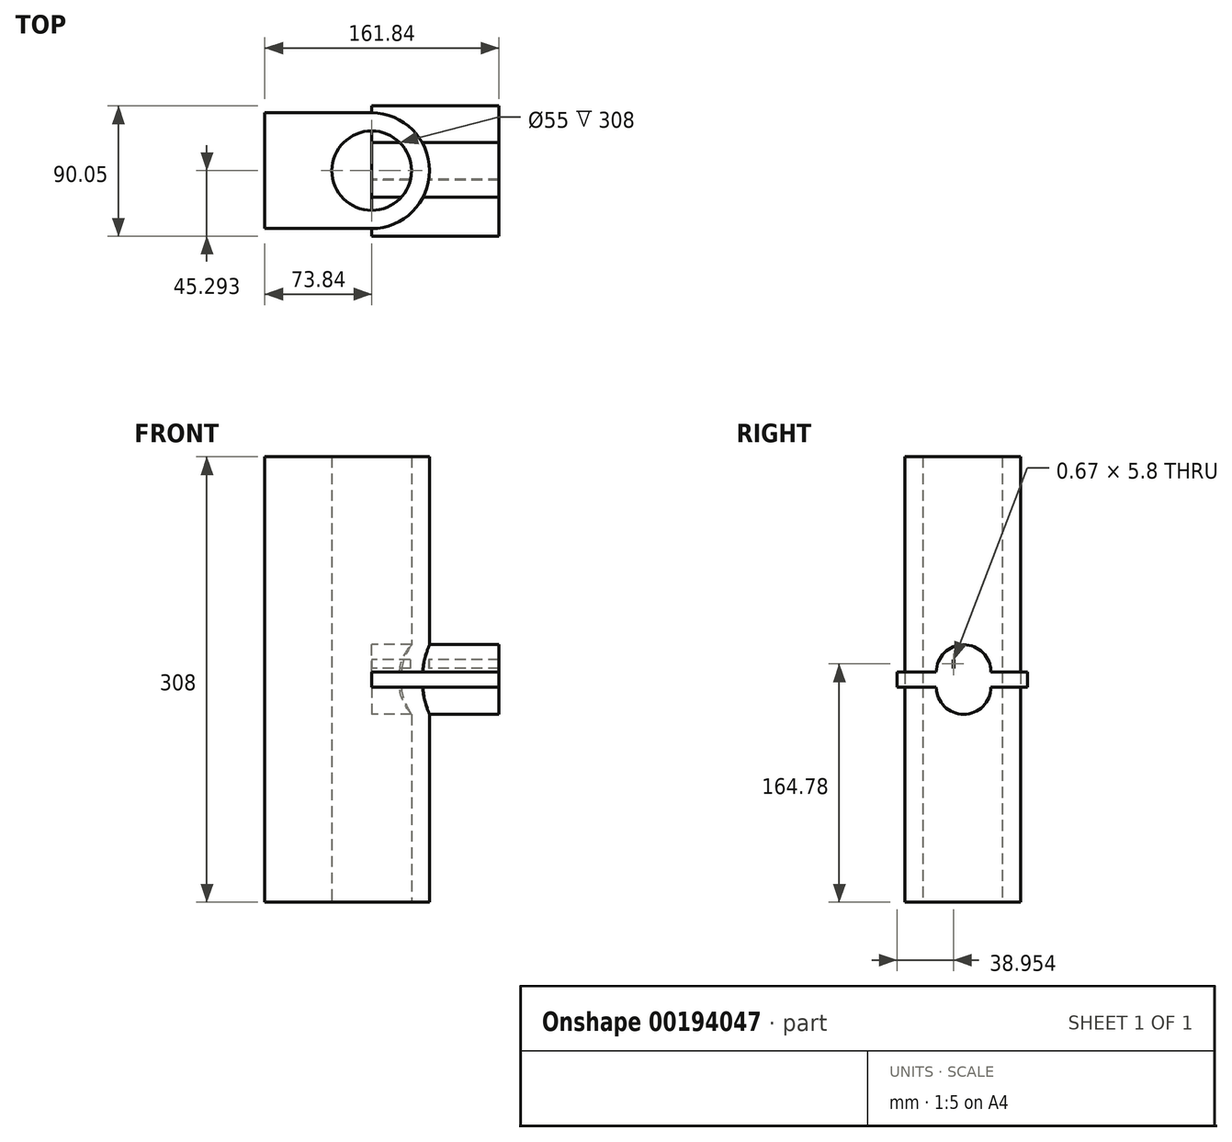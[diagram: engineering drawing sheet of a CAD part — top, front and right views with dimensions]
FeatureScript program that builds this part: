
annotation { "Feature Type Name" : "Feature", "Feature Type Description" : "" }
export const myFeature = defineFeature(function(context is Context, id is Id, definition is map)
    precondition{}
    {
        {
            var Q0;
            Q0=qCreatedBy(makeId("Top.planeOp"),FACE);
            var sketch = newSketch(context, id + "F0", { "sketchPlane" : qUnion([Q0])});
            skLineSegment(sketch, "E0.bottom", {"start": v(-73.84, 71.78) * mm, "end": v(0, 71.78) * mm});
            skLineSegment(sketch, "E0.top", {"start": v(-73.84, -8.22) * mm, "end": v(0, -8.22) * mm});
            skLineSegment(sketch, "E0.left", {"start": v(-73.84, 71.78) * mm, "end": v(-73.84, -8.22) * mm});
            skLineSegment(sketch, "E0.right", {"start": v(0, 71.78) * mm, "end": v(0, -8.22) * mm});
            skArc(sketch, "E1", {"start": v(0, 71.78) * mm, "mid": v(40, 31.78) * mm, "end": v(0, -8.22) * mm});
            skCircle(sketch, "E2", {"center": v(0, 31.78) * mm, "radius": 27.5 * mm});
            skSolve(sketch);
        }
        {
            var Q0;
            {var subQ0=sQuery(id+"F0.wireOp",EDGE,"E2");var subQ1=sQuery(id+"F0.wireOp",EDGE,"E0.right");var subQ2=makeQuery(id+"F0.imprint","INTERSECT",VERTEX,{"disambiguationData":[OD(0.0)],"derivedFrom":[subQ1,subQ0]});Q0=makeQuery(id+"F0.imprint","IMPRINT",FACE,{"disambiguationData":[TD([[makeQuery(id+"F0.imprint","IMPRINT",EDGE,{"disambiguationData":[TD([[subQ2,-1.0]])],"derivedFrom":subQ1}),1.0]])]});}
            var Q1;
            {var subQ0=sQuery(id+"F0.wireOp",EDGE,"E2");var subQ1=sQuery(id+"F0.wireOp",EDGE,"E0.right");var subQ2=makeQuery(id+"F0.imprint","INTERSECT",VERTEX,{"disambiguationData":[OD(0.0)],"derivedFrom":[subQ1,subQ0]});Q1=makeQuery(id+"F0.imprint","IMPRINT",FACE,{"disambiguationData":[TD([[makeQuery(id+"F0.imprint","IMPRINT",EDGE,{"disambiguationData":[TD([[subQ2,-1.0]])],"derivedFrom":subQ1}),-1.0]])]});}
            extrude(context, id + "F1", {"entities" : qUnion([Q0, Q1]), "endBound" : BoundingType.SYMMETRIC, "depth" : 220 * mm});
        }
        {
            var Q0;
            Q0=qCreatedBy(makeId("Right.planeOp"),FACE);
            var sketch = newSketch(context, id + "F2", { "sketchPlane" : qUnion([Q0])});
            skLineSegment(sketch, "E3.bottom", {"start": v(43.22, 172.21) * mm, "end": v(42.77, 172.21) * mm});
            skLineSegment(sketch, "E3.top", {"start": v(43.22, 182.57) * mm, "end": v(42.77, 182.57) * mm});
            skLineSegment(sketch, "E4.bottom", {"start": v(-13.5, 5.18) * mm, "end": v(13.5, 5.18) * mm});
            skLineSegment(sketch, "E4.top", {"start": v(-13.5, -5.18) * mm, "end": v(13.5, -5.18) * mm});
            skLineSegment(sketch, "E4.left", {"start": v(-13.5, 5.18) * mm, "end": v(-13.5, -5.18) * mm});
            skLineSegment(sketch, "E4.right", {"start": v(13.5, 5.18) * mm, "end": v(13.5, -5.18) * mm});
            skPoint(sketch, "E4.middle", {"position": v(0, 0) * mm});
            skLineSegment(sketch, "E5.bottom", {"start": v(76.54, 5.18) * mm, "end": v(51.33, 5.18) * mm});
            skLineSegment(sketch, "E5.top", {"start": v(76.54, -5.18) * mm, "end": v(51.33, -5.18) * mm});
            skLineSegment(sketch, "E5.left", {"start": v(76.54, 5.18) * mm, "end": v(76.54, -5.18) * mm});
            skLineSegment(sketch, "E5.right", {"start": v(51.33, 5.18) * mm, "end": v(51.33, -5.18) * mm});
            skPoint(sketch, "E5.middle", {"position": v(63.93, 0) * mm});
            skArc(sketch, "E6", {"start": v(13.5, 5.18) * mm, "mid": v(32.42, 24.09) * mm, "end": v(51.33, 5.18) * mm});
            skArc(sketch, "E7", {"start": v(13.5, -5.18) * mm, "mid": v(31.63, 3.85) * mm, "end": v(32.42, 24.09) * mm});
            skArc(sketch, "E8", {"start": v(32.42, 24.09) * mm, "mid": v(33.2, 3.85) * mm, "end": v(51.33, -5.18) * mm});
            skArc(sketch, "E9", {"start": v(13.5, -5.18) * mm, "mid": v(32.42, -24.09) * mm, "end": v(51.33, -5.18) * mm});
            skText(sketch, "E10", { "text": "I", "fontName": "OpenSans-Regular.ttf"});
            const initialGuessF2  = {"E10": [0.02431, 0.00788, 1, 0, 0.00585]};
            skSetInitialGuess(sketch, initialGuessF2);
            skSolve(sketch);
        }
        {
            var Q0;
            {var subQ2=sQuery(id+"F0.wireOp",EDGE,"E0.top");Q0=makeQuery(id+"F0.imprint","IMPRINT",FACE,{"disambiguationData":[TD([[makeQuery(id+"F0.imprint","IMPRINT",EDGE,{"derivedFrom":subQ2}),1.0]])]});}
            var Q1;
            {var subQ0=sQuery(id+"F0.wireOp",EDGE,"E1");Q1=makeQuery(id+"F0.imprint","IMPRINT",FACE,{"disambiguationData":[TD([[makeQuery(id+"F0.imprint","IMPRINT",EDGE,{"derivedFrom":subQ0}),-1.0]])]});}
            var Q2;
            Q2=makeQuery(id+"F1.opExtrude","CAP_FACE",FACE,{"disambiguationData":[OSD([sQuery(id+"F0.wireOp",EDGE,"E2")])],"isStart":true});
            var Q3;
            Q3=makeQuery(id+"F1.opExtrude","CAP_FACE",FACE,{"disambiguationData":[OSD([sQuery(id+"F0.wireOp",EDGE,"E2")])],"isStart":false});
            extrude(context, id + "F3", {"entities" : qUnion([Q0, Q1, Q2, Q3]), "operationType" : NewBodyOperationType.ADD, "endBound" : BoundingType.SYMMETRIC, "depth" : 88 * mm});
        }
        {
            var Q0;
            Q0 = qSketchRegion(id + "F2", true);
            extrude(context, id + "F4", {"entities" : qUnion([Q0]), "operationType" : NewBodyOperationType.ADD, "depth" : 88 * mm});
        }
    });
